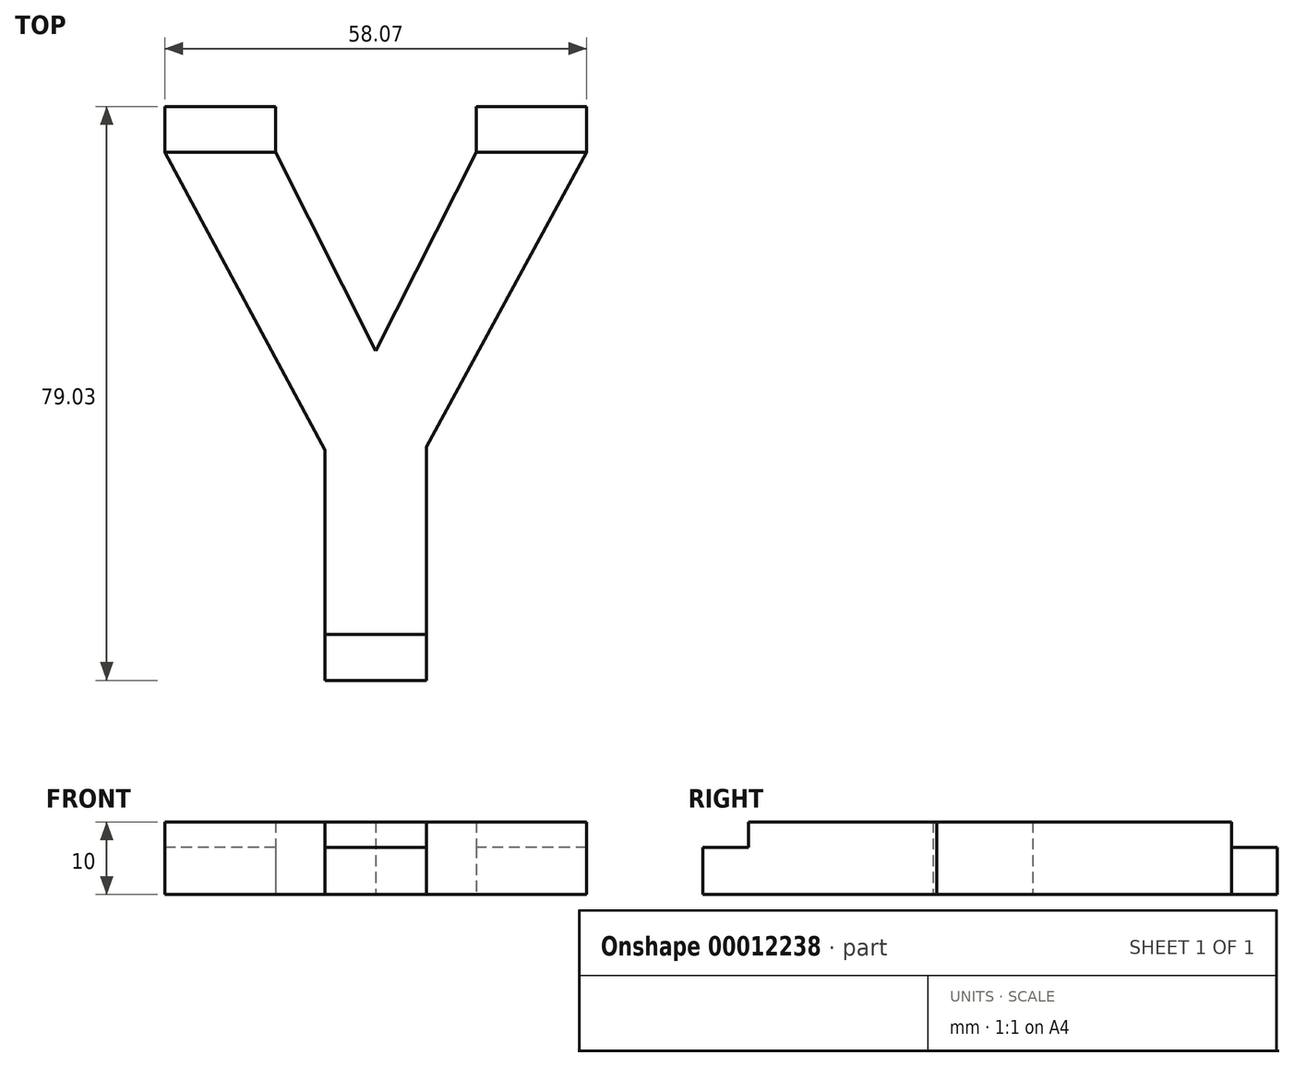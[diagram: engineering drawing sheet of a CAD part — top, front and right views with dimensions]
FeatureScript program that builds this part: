
annotation { "Feature Type Name" : "Feature", "Feature Type Description" : "" }
export const myFeature = defineFeature(function(context is Context, id is Id, definition is map)
    precondition{}
    {
        {
            var Q0;
            Q0=qCreatedBy(makeId("Top.planeOp"),FACE);
            var sketch = newSketch(context, id + "F0", { "sketchPlane" : qUnion([Q0])});
            skText(sketch, "E0", { "text": "Y", "fontName": "OpenSans-Bold.ttf"});
            const initialGuessF0  = {"E0": [-0.05807, 0, 1, 0, 0.067]};
            skSetInitialGuess(sketch, initialGuessF0);
            skSolve(sketch);
        }
        {
            var Q0;
            Q0=makeQuery(id+"F0.imprint","IMPRINT",FACE,{"disambiguationData":[TD([[makeQuery(id+"F0.imprint","IMPRINT",EDGE,{"derivedFrom":sQuery(id+"F0.wireOp",EDGE,"E0.sketch_text.stroke-0")}),-1.0]])]});
            extrude(context, id + "F1", {"entities" : qUnion([Q0]), "depth" : 10 * mm});
        }
        {
            var Q0;
            Q0=makeQuery(id+"F1.opExtrude","SWEPT_FACE",FACE,{"disambiguationData":[OSD([sQuery(id+"F0.wireOp",EDGE,"E0.sketch_text.stroke-4")])]});
            var sketch = newSketch(context, id + "F2", { "sketchPlane" : qUnion([Q0])});
            skLineSegment(sketch, "E1.0.0", {"start": v(-36.03, 0) * mm, "end": v(-22.04, 0) * mm});
            skLineSegment(sketch, "E1.0.1", {"start": v(-22.04, 0) * mm, "end": v(-22.04, 10) * mm});
            skLineSegment(sketch, "E1.0.2", {"start": v(-22.04, 10) * mm, "end": v(-36.03, 10) * mm});
            skLineSegment(sketch, "E1.0.3", {"start": v(-36.03, 10) * mm, "end": v(-36.03, 0) * mm});
            skLineSegment(sketch, "E2.top", {"start": v(-36.03, 6.5) * mm, "end": v(-22.04, 6.5) * mm});
            skLineSegment(sketch, "E2.left", {"start": v(-36.03, 0) * mm, "end": v(-36.03, 6.5) * mm});
            skLineSegment(sketch, "E2.right", {"start": v(-22.04, 0) * mm, "end": v(-22.04, 6.5) * mm});
            skSolve(sketch);
        }
        {
            var Q0;
            Q0=makeQuery(id+"F2.imprint","IMPRINT",FACE,{"disambiguationData":[TD([[makeQuery(id+"F2.imprint","IMPRINT",EDGE,{"derivedFrom":sQuery(id+"F2.wireOp",EDGE,"E1.0.0")}),-1.0]])]});
            extrude(context, id + "F3", {"entities" : qUnion([Q0]), "operationType" : NewBodyOperationType.ADD, "depth" : 6.3 * mm});
        }
        {
            var Q0;
            Q0=makeQuery(id+"F1.opExtrude","SWEPT_FACE",FACE,{"disambiguationData":[OSD([sQuery(id+"F0.wireOp",EDGE,"E0.sketch_text.stroke-1")])]});
            var sketch = newSketch(context, id + "F4", { "sketchPlane" : qUnion([Q0])});
            skLineSegment(sketch, "E3.0.0", {"start": v(0, 0) * mm, "end": v(15.18, 0) * mm});
            skLineSegment(sketch, "E3.0.1", {"start": v(15.18, 0) * mm, "end": v(15.18, 10) * mm});
            skLineSegment(sketch, "E3.0.2", {"start": v(15.18, 10) * mm, "end": v(0, 10) * mm});
            skLineSegment(sketch, "E3.0.3", {"start": v(0, 10) * mm, "end": v(0, 0) * mm});
            skLineSegment(sketch, "E4.0.0", {"start": v(42.8, 0) * mm, "end": v(58.07, 0) * mm});
            skLineSegment(sketch, "E4.0.1", {"start": v(58.07, 0) * mm, "end": v(58.07, 10) * mm});
            skLineSegment(sketch, "E4.0.2", {"start": v(58.07, 10) * mm, "end": v(42.8, 10) * mm});
            skLineSegment(sketch, "E4.0.3", {"start": v(42.8, 10) * mm, "end": v(42.8, 0) * mm});
            skLineSegment(sketch, "E5.top", {"start": v(0, 6.5) * mm, "end": v(15.18, 6.5) * mm});
            skLineSegment(sketch, "E5.left", {"start": v(0, 0) * mm, "end": v(0, 6.5) * mm});
            skLineSegment(sketch, "E5.right", {"start": v(15.18, 0) * mm, "end": v(15.18, 6.5) * mm});
            skLineSegment(sketch, "E6.top", {"start": v(42.8, 6.5) * mm, "end": v(58.07, 6.5) * mm});
            skLineSegment(sketch, "E6.left", {"start": v(42.8, 0) * mm, "end": v(42.8, 6.5) * mm});
            skLineSegment(sketch, "E6.right", {"start": v(58.07, 0) * mm, "end": v(58.07, 6.5) * mm});
            skSolve(sketch);
        }
        {
            var Q0;
            Q0=makeQuery(id+"F4.imprint","IMPRINT",FACE,{"disambiguationData":[TD([[makeQuery(id+"F4.imprint","IMPRINT",EDGE,{"derivedFrom":sQuery(id+"F4.wireOp",EDGE,"E3.0.0")}),-1.0]])]});
            var Q1;
            Q1=makeQuery(id+"F4.imprint","IMPRINT",FACE,{"disambiguationData":[TD([[makeQuery(id+"F4.imprint","IMPRINT",EDGE,{"derivedFrom":sQuery(id+"F4.wireOp",EDGE,"E4.0.0")}),1.0]])]});
            extrude(context, id + "F5", {"entities" : qUnion([Q0, Q1]), "operationType" : NewBodyOperationType.ADD, "depth" : 6.3 * mm});
        }
    });
